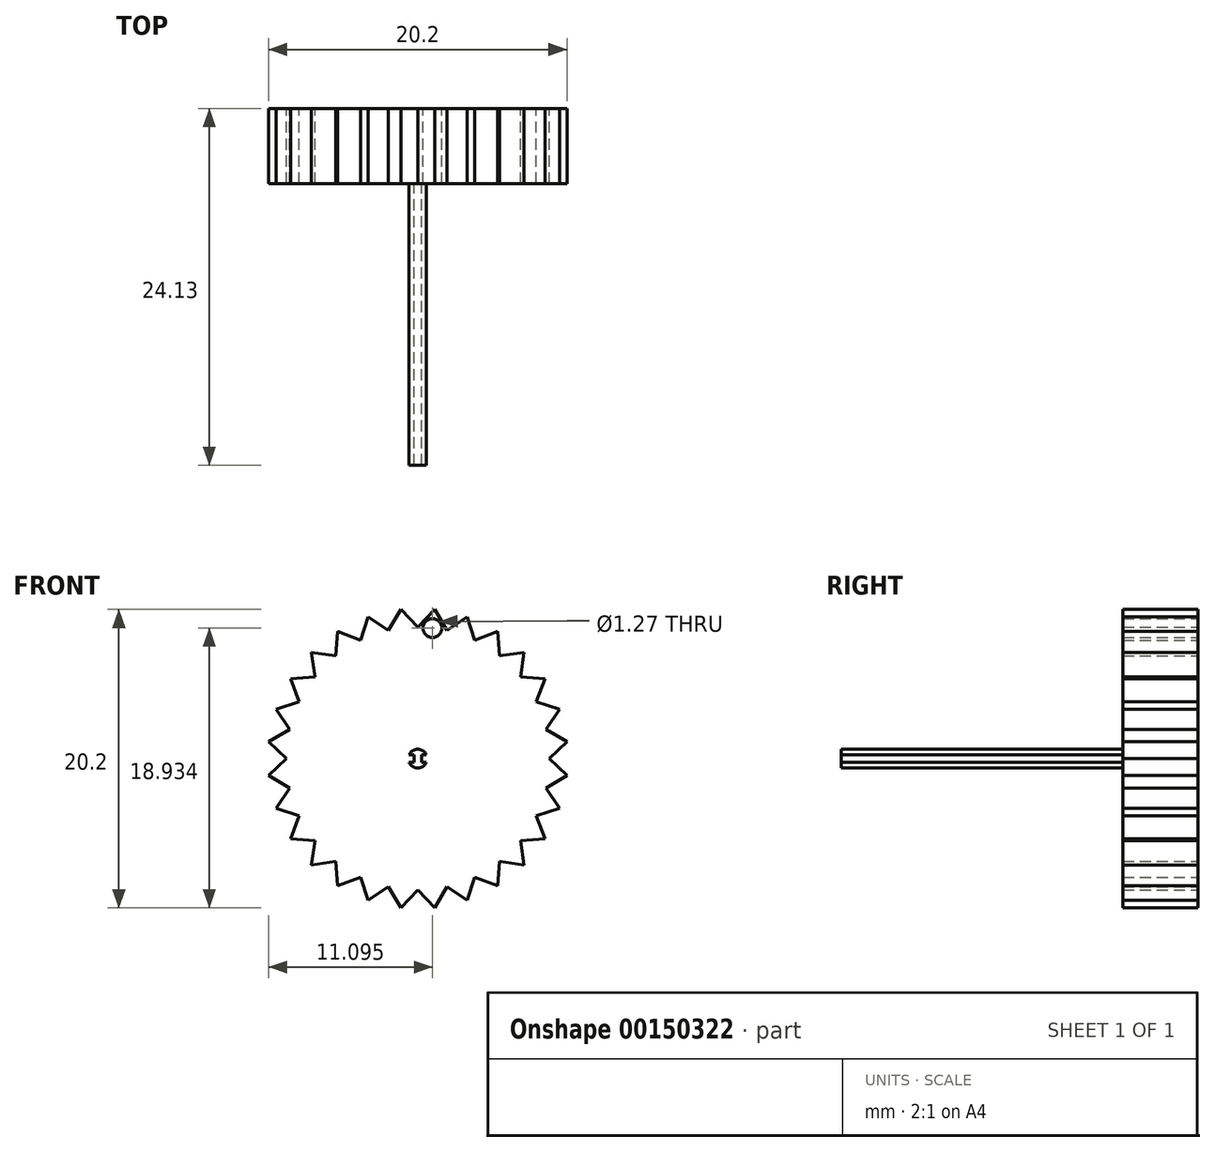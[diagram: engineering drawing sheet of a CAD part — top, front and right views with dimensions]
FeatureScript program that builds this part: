
annotation { "Feature Type Name" : "Feature", "Feature Type Description" : "" }
export const myFeature = defineFeature(function(context is Context, id is Id, definition is map)
    precondition{}
    {
        {
            var Q0;
            Q0=qCreatedBy(makeId("Front.planeOp"),FACE);
            var sketch = newSketch(context, id + "F0", { "sketchPlane" : qUnion([Q0])});
            skCircle(sketch, "E0", {"center": v(0, 0) * mm, "radius": 10.16 * mm});
            skCircle(sketch, "E1", {"center": v(0, 0) * mm, "radius": 8.9 * mm});
            skLineSegment(sketch, "E2", {"start": v(0, 0) * mm, "end": v(0, 8.9) * mm});
            skLineSegment(sketch, "E3", {"start": v(0, 8.9) * mm, "end": v(0, -8.9) * mm});
            skLineSegment(sketch, "E4", {"start": v(0, -8.9) * mm, "end": v(-1.14, -10.1) * mm});
            skLineSegment(sketch, "E5", {"start": v(-1.14, -10.1) * mm, "end": v(-1.98, -8.67) * mm});
            skLineSegment(sketch, "E6", {"start": v(-1.98, -8.67) * mm, "end": v(0, 0) * mm});
            skLineSegment(sketch, "E7", {"start": v(-1.14, -10.1) * mm, "end": v(0, 0) * mm});
            skLineSegment(sketch, "E8", {"start": v(0, 0) * mm, "end": v(-3.36, -9.59) * mm});
            skLineSegment(sketch, "E9", {"start": v(0, 0) * mm, "end": v(-3.86, -8) * mm});
            skLineSegment(sketch, "E10", {"start": v(-3.86, -8) * mm, "end": v(-3.36, -9.59) * mm});
            skLineSegment(sketch, "E11", {"start": v(-1.98, -8.67) * mm, "end": v(-3.36, -9.59) * mm});
            skLineSegment(sketch, "E12.MirrorCS", {"start": v(-3.86, -8) * mm, "end": v(-5.4, -8.6) * mm});
            skLineSegment(sketch, "E13.MirrorCS", {"start": v(0, 0) * mm, "end": v(-5.4, -8.6) * mm});
            skLineSegment(sketch, "E14.MirrorCS", {"start": v(-5.54, -6.95) * mm, "end": v(-5.4, -8.6) * mm});
            skLineSegment(sketch, "E15.MirrorCS", {"start": v(-7.18, -7.18) * mm, "end": v(-5.54, -6.95) * mm});
            skLineSegment(sketch, "E16.MirrorCS", {"start": v(-5.54, -6.95) * mm, "end": v(0, 0) * mm});
            skLineSegment(sketch, "E17.MirrorCS", {"start": v(-7.18, -7.18) * mm, "end": v(0, 0) * mm});
            skLineSegment(sketch, "E18.MirrorCS", {"start": v(-6.95, -5.54) * mm, "end": v(-7.18, -7.18) * mm});
            skLineSegment(sketch, "E19.MirrorCS", {"start": v(6.95, 5.54) * mm, "end": v(-6.95, -5.54) * mm});
            skLineSegment(sketch, "E20.MirrorCS", {"start": v(-6.95, -5.54) * mm, "end": v(-8.6, -5.4) * mm});
            skLineSegment(sketch, "E21.MirrorCS", {"start": v(-8.6, -5.4) * mm, "end": v(0, 0) * mm});
            skLineSegment(sketch, "E22.MirrorCS", {"start": v(-8.6, -5.4) * mm, "end": v(-8, -3.86) * mm});
            skLineSegment(sketch, "E23.MirrorCS", {"start": v(-8, -3.86) * mm, "end": v(0, 0) * mm});
            skLineSegment(sketch, "E24.MirrorCS", {"start": v(-8, -3.86) * mm, "end": v(-9.59, -3.36) * mm});
            skLineSegment(sketch, "E25.MirrorCS", {"start": v(0, 0) * mm, "end": v(-9.59, -3.36) * mm});
            skLineSegment(sketch, "E26.MirrorCS", {"start": v(-8.67, -1.98) * mm, "end": v(-9.59, -3.36) * mm});
            skLineSegment(sketch, "E27.MirrorCS", {"start": v(0, 0) * mm, "end": v(-8.67, -1.98) * mm});
            skLineSegment(sketch, "E28.MirrorCS", {"start": v(-8.67, -1.98) * mm, "end": v(-10.1, -1.14) * mm});
            skLineSegment(sketch, "E29.MirrorCS", {"start": v(0, 0) * mm, "end": v(-10.1, -1.14) * mm});
            skLineSegment(sketch, "E30.MirrorCS", {"start": v(-8.9, 0) * mm, "end": v(-10.1, -1.14) * mm});
            skLineSegment(sketch, "E31.MirrorCS", {"start": v(-8.9, 0) * mm, "end": v(0, 0) * mm});
            skLineSegment(sketch, "E32.MirrorCS", {"start": v(-10.1, 1.14) * mm, "end": v(-8.9, 0) * mm});
            skLineSegment(sketch, "E33.MirrorCS", {"start": v(-10.1, 1.14) * mm, "end": v(0, 0) * mm});
            skLineSegment(sketch, "E34.MirrorCS", {"start": v(-8.67, 1.98) * mm, "end": v(-10.1, 1.14) * mm});
            skLineSegment(sketch, "E35.MirrorCS", {"start": v(8.67, -1.98) * mm, "end": v(-8.67, 1.98) * mm});
            skLineSegment(sketch, "E36.MirrorCS", {"start": v(-8.67, 1.98) * mm, "end": v(-9.59, 3.36) * mm});
            skLineSegment(sketch, "E37.MirrorCS", {"start": v(-9.59, 3.36) * mm, "end": v(0, 0) * mm});
            skLineSegment(sketch, "E38.MirrorCS", {"start": v(-9.59, 3.36) * mm, "end": v(-8, 3.86) * mm});
            skLineSegment(sketch, "E39.MirrorCS", {"start": v(-8, 3.86) * mm, "end": v(0, 0) * mm});
            skLineSegment(sketch, "E40.MirrorCS", {"start": v(-8, 3.86) * mm, "end": v(-8.6, 5.4) * mm});
            skLineSegment(sketch, "E41.MirrorCS", {"start": v(0, 0) * mm, "end": v(-8.6, 5.4) * mm});
            skLineSegment(sketch, "E42.MirrorCS", {"start": v(-6.95, 5.54) * mm, "end": v(-8.6, 5.4) * mm});
            skLineSegment(sketch, "E43.MirrorCS", {"start": v(0, 0) * mm, "end": v(-6.95, 5.54) * mm});
            skLineSegment(sketch, "E44.MirrorCS", {"start": v(-6.95, 5.54) * mm, "end": v(-7.18, 7.18) * mm});
            skLineSegment(sketch, "E45.MirrorCS", {"start": v(0, 0) * mm, "end": v(-7.18, 7.18) * mm});
            skLineSegment(sketch, "E46.MirrorCS", {"start": v(-5.54, 6.95) * mm, "end": v(-7.18, 7.18) * mm});
            skLineSegment(sketch, "E47.MirrorCS", {"start": v(-5.54, 6.95) * mm, "end": v(0, 0) * mm});
            skLineSegment(sketch, "E48.MirrorCS", {"start": v(-5.4, 8.6) * mm, "end": v(-5.54, 6.95) * mm});
            skLineSegment(sketch, "E49.MirrorCS", {"start": v(-5.4, 8.6) * mm, "end": v(0, 0) * mm});
            skLineSegment(sketch, "E50.MirrorCS", {"start": v(-3.86, 8) * mm, "end": v(-5.4, 8.6) * mm});
            skLineSegment(sketch, "E51.MirrorCS", {"start": v(3.86, -8) * mm, "end": v(-3.86, 8) * mm});
            skLineSegment(sketch, "E52.MirrorCS", {"start": v(-3.86, 8) * mm, "end": v(-3.36, 9.59) * mm});
            skLineSegment(sketch, "E53.MirrorCS", {"start": v(-3.36, 9.59) * mm, "end": v(0, 0) * mm});
            skLineSegment(sketch, "E54.MirrorCS", {"start": v(-3.36, 9.59) * mm, "end": v(-1.98, 8.67) * mm});
            skLineSegment(sketch, "E55.MirrorCS", {"start": v(-1.98, 8.67) * mm, "end": v(0, 0) * mm});
            skLineSegment(sketch, "E56.MirrorCS", {"start": v(-1.98, 8.67) * mm, "end": v(-1.14, 10.1) * mm});
            skLineSegment(sketch, "E57.MirrorCS", {"start": v(0, 0) * mm, "end": v(-1.14, 10.1) * mm});
            skLineSegment(sketch, "E58.MirrorCS", {"start": v(0, 8.89) * mm, "end": v(-1.14, 10.1) * mm});
            skLineSegment(sketch, "E59.MirrorCS", {"start": v(0, 0) * mm, "end": v(0, 8.89) * mm});
            skLineSegment(sketch, "E60.MirrorCS", {"start": v(0, 8.89) * mm, "end": v(1.14, 10.1) * mm});
            skLineSegment(sketch, "E61.MirrorCS", {"start": v(0, 0) * mm, "end": v(1.14, 10.1) * mm});
            skLineSegment(sketch, "E62.MirrorCS", {"start": v(1.98, 8.67) * mm, "end": v(1.14, 10.1) * mm});
            skLineSegment(sketch, "E63.MirrorCS", {"start": v(1.98, 8.67) * mm, "end": v(0, 0) * mm});
            skLineSegment(sketch, "E64.MirrorCS", {"start": v(3.36, 9.59) * mm, "end": v(1.98, 8.67) * mm});
            skLineSegment(sketch, "E65.MirrorCS", {"start": v(3.36, 9.59) * mm, "end": v(0, 0) * mm});
            skLineSegment(sketch, "E66.MirrorCS", {"start": v(3.86, 8) * mm, "end": v(3.36, 9.59) * mm});
            skLineSegment(sketch, "E67.MirrorCS", {"start": v(-3.86, -8) * mm, "end": v(3.86, 8) * mm});
            skLineSegment(sketch, "E68.MirrorCS", {"start": v(3.86, 8) * mm, "end": v(5.4, 8.6) * mm});
            skLineSegment(sketch, "E69.MirrorCS", {"start": v(5.4, 8.6) * mm, "end": v(0, 0) * mm});
            skLineSegment(sketch, "E70.MirrorCS", {"start": v(5.4, 8.6) * mm, "end": v(5.54, 6.95) * mm});
            skLineSegment(sketch, "E71.MirrorCS", {"start": v(5.54, 6.95) * mm, "end": v(0, 0) * mm});
            skLineSegment(sketch, "E72.MirrorCS", {"start": v(5.54, 6.95) * mm, "end": v(7.18, 7.18) * mm});
            skLineSegment(sketch, "E73.MirrorCS", {"start": v(0, 0) * mm, "end": v(7.18, 7.18) * mm});
            skLineSegment(sketch, "E74.MirrorCS", {"start": v(6.95, 5.54) * mm, "end": v(7.18, 7.18) * mm});
            skLineSegment(sketch, "E75.MirrorCS", {"start": v(6.95, 5.54) * mm, "end": v(8.6, 5.4) * mm});
            skLineSegment(sketch, "E76.MirrorCS", {"start": v(0, 0) * mm, "end": v(8.6, 5.4) * mm});
            skLineSegment(sketch, "E77.MirrorCS", {"start": v(8, 3.86) * mm, "end": v(8.6, 5.4) * mm});
            skLineSegment(sketch, "E78.MirrorCS", {"start": v(8, 3.86) * mm, "end": v(0, 0) * mm});
            skLineSegment(sketch, "E79.MirrorCS", {"start": v(9.59, 3.36) * mm, "end": v(8, 3.86) * mm});
            skLineSegment(sketch, "E80.MirrorCS", {"start": v(9.59, 3.36) * mm, "end": v(0, 0) * mm});
            skLineSegment(sketch, "E81.MirrorCS", {"start": v(8.67, 1.98) * mm, "end": v(9.59, 3.36) * mm});
            skLineSegment(sketch, "E82.MirrorCS", {"start": v(-8.67, -1.98) * mm, "end": v(8.67, 1.98) * mm});
            skLineSegment(sketch, "E83.MirrorCS", {"start": v(8.67, 1.98) * mm, "end": v(10.1, 1.14) * mm});
            skLineSegment(sketch, "E84.MirrorCS", {"start": v(10.1, 1.14) * mm, "end": v(8.9, 0) * mm});
            skLineSegment(sketch, "E85.MirrorCS", {"start": v(10.1, 1.14) * mm, "end": v(0, 0) * mm});
            skLineSegment(sketch, "E86.MirrorCS", {"start": v(8.9, 0) * mm, "end": v(0, 0) * mm});
            skLineSegment(sketch, "E87.MirrorCS", {"start": v(8.9, 0) * mm, "end": v(10.1, -1.14) * mm});
            skLineSegment(sketch, "E88.MirrorCS", {"start": v(0, 0) * mm, "end": v(10.1, -1.14) * mm});
            skLineSegment(sketch, "E89.MirrorCS", {"start": v(8.67, -1.98) * mm, "end": v(10.1, -1.14) * mm});
            skLineSegment(sketch, "E90.MirrorCS", {"start": v(0, 0) * mm, "end": v(8.67, -1.98) * mm});
            skLineSegment(sketch, "E91.MirrorCS", {"start": v(8.67, -1.98) * mm, "end": v(9.59, -3.36) * mm});
            skLineSegment(sketch, "E92.MirrorCS", {"start": v(0, 0) * mm, "end": v(9.59, -3.36) * mm});
            skLineSegment(sketch, "E93.MirrorCS", {"start": v(8, -3.86) * mm, "end": v(9.59, -3.36) * mm});
            skLineSegment(sketch, "E94.MirrorCS", {"start": v(8, -3.86) * mm, "end": v(0, 0) * mm});
            skLineSegment(sketch, "E95.MirrorCS", {"start": v(8.6, -5.4) * mm, "end": v(8, -3.86) * mm});
            skLineSegment(sketch, "E96.MirrorCS", {"start": v(8.6, -5.4) * mm, "end": v(0, 0) * mm});
            skLineSegment(sketch, "E97.MirrorCS", {"start": v(6.95, -5.54) * mm, "end": v(8.6, -5.4) * mm});
            skLineSegment(sketch, "E98.MirrorCS", {"start": v(-6.95, 5.54) * mm, "end": v(6.95, -5.54) * mm});
            skLineSegment(sketch, "E99.MirrorCS", {"start": v(6.95, -5.54) * mm, "end": v(7.18, -7.18) * mm});
            skLineSegment(sketch, "E100.MirrorCS", {"start": v(7.18, -7.18) * mm, "end": v(0, 0) * mm});
            skLineSegment(sketch, "E101.MirrorCS", {"start": v(7.18, -7.18) * mm, "end": v(5.54, -6.95) * mm});
            skLineSegment(sketch, "E102.MirrorCS", {"start": v(5.54, -6.95) * mm, "end": v(0, 0) * mm});
            skLineSegment(sketch, "E103.MirrorCS", {"start": v(5.54, -6.95) * mm, "end": v(5.4, -8.6) * mm});
            skLineSegment(sketch, "E104.MirrorCS", {"start": v(0, 0) * mm, "end": v(5.4, -8.6) * mm});
            skLineSegment(sketch, "E105.MirrorCS", {"start": v(3.86, -8) * mm, "end": v(5.4, -8.6) * mm});
            skLineSegment(sketch, "E106.MirrorCS", {"start": v(0, 0) * mm, "end": v(3.86, -8) * mm});
            skLineSegment(sketch, "E107.MirrorCS", {"start": v(3.86, -8) * mm, "end": v(3.36, -9.59) * mm});
            skLineSegment(sketch, "E108.MirrorCS", {"start": v(1.98, -8.67) * mm, "end": v(3.36, -9.59) * mm});
            skLineSegment(sketch, "E109.MirrorCS", {"start": v(0, 0) * mm, "end": v(3.36, -9.59) * mm});
            skLineSegment(sketch, "E110.MirrorCS", {"start": v(1.98, -8.67) * mm, "end": v(0, 0) * mm});
            skLineSegment(sketch, "E111.MirrorCS", {"start": v(1.14, -10.1) * mm, "end": v(1.98, -8.67) * mm});
            skLineSegment(sketch, "E112.MirrorCS", {"start": v(1.14, -10.1) * mm, "end": v(0, 0) * mm});
            skLineSegment(sketch, "E113.MirrorCS", {"start": v(0, -8.9) * mm, "end": v(1.14, -10.1) * mm});
            skSolve(sketch);
        }
        {
            var Q0;
            {var subQ0=sQuery(id+"F0.wireOp",EDGE,"E51.MirrorCS");Q0=makeQuery(id+"F0.imprint","IMPRINT",FACE,{"disambiguationData":[TD([[makeQuery(id+"F0.imprint","IMPRINT",EDGE,{"derivedFrom":subQ0}),1.0]])]});}
            var Q1;
            {var subQ0=sQuery(id+"F0.wireOp",EDGE,"E47.MirrorCS");Q1=makeQuery(id+"F0.imprint","IMPRINT",FACE,{"disambiguationData":[TD([[makeQuery(id+"F0.imprint","IMPRINT",EDGE,{"derivedFrom":subQ0}),1.0]])]});}
            var Q2;
            {var subQ0=sQuery(id+"F0.wireOp",EDGE,"E48.MirrorCS");Q2=makeQuery(id+"F0.imprint","IMPRINT",FACE,{"disambiguationData":[TD([[makeQuery(id+"F0.imprint","IMPRINT",EDGE,{"derivedFrom":subQ0}),1.0]])]});}
            var Q3;
            {var subQ0=sQuery(id+"F0.wireOp",EDGE,"E50.MirrorCS");Q3=makeQuery(id+"F0.imprint","IMPRINT",FACE,{"disambiguationData":[TD([[makeQuery(id+"F0.imprint","IMPRINT",EDGE,{"derivedFrom":subQ0}),1.0]])]});}
            var Q4;
            {var subQ0=sQuery(id+"F0.wireOp",EDGE,"E52.MirrorCS");Q4=makeQuery(id+"F0.imprint","IMPRINT",FACE,{"disambiguationData":[TD([[makeQuery(id+"F0.imprint","IMPRINT",EDGE,{"derivedFrom":subQ0}),-1.0]])]});}
            var Q5;
            {var subQ0=sQuery(id+"F0.wireOp",EDGE,"E54.MirrorCS");Q5=makeQuery(id+"F0.imprint","IMPRINT",FACE,{"disambiguationData":[TD([[makeQuery(id+"F0.imprint","IMPRINT",EDGE,{"derivedFrom":subQ0}),-1.0]])]});}
            var Q6;
            {var subQ0=sQuery(id+"F0.wireOp",EDGE,"E55.MirrorCS");Q6=makeQuery(id+"F0.imprint","IMPRINT",FACE,{"disambiguationData":[TD([[makeQuery(id+"F0.imprint","IMPRINT",EDGE,{"derivedFrom":subQ0}),-1.0]])]});}
            var Q7;
            {var subQ0=sQuery(id+"F0.wireOp",EDGE,"E51.MirrorCS");Q7=makeQuery(id+"F0.imprint","IMPRINT",FACE,{"disambiguationData":[TD([[makeQuery(id+"F0.imprint","IMPRINT",EDGE,{"derivedFrom":subQ0}),-1.0]])]});}
            var Q8;
            {var subQ1=sQuery(id+"F0.wireOp",EDGE,"E1");var subQ3=sQuery(id+"F0.wireOp",EDGE,"E57.MirrorCS");var subQ4=makeQuery(id+"F0.imprint","INTERSECT",VERTEX,{"derivedFrom":[subQ1,subQ3]});Q8=makeQuery(id+"F0.imprint","IMPRINT",FACE,{"disambiguationData":[TD([[makeQuery(id+"F0.imprint","IMPRINT",EDGE,{"disambiguationData":[TD([[subQ4,1.0]])],"derivedFrom":subQ1}),1.0]])]});}
            var Q9;
            {var subQ0=sQuery(id+"F0.wireOp",EDGE,"E58.MirrorCS");Q9=makeQuery(id+"F0.imprint","IMPRINT",FACE,{"disambiguationData":[TD([[makeQuery(id+"F0.imprint","IMPRINT",EDGE,{"derivedFrom":subQ0}),1.0]])]});}
            var Q10;
            {var subQ0=sQuery(id+"F0.wireOp",EDGE,"E56.MirrorCS");Q10=makeQuery(id+"F0.imprint","IMPRINT",FACE,{"disambiguationData":[TD([[makeQuery(id+"F0.imprint","IMPRINT",EDGE,{"derivedFrom":subQ0}),-1.0]])]});}
            var Q11;
            {var subQ0=sQuery(id+"F0.wireOp",EDGE,"E55.MirrorCS");Q11=makeQuery(id+"F0.imprint","IMPRINT",FACE,{"disambiguationData":[TD([[makeQuery(id+"F0.imprint","IMPRINT",EDGE,{"derivedFrom":subQ0}),1.0]])]});}
            var Q12;
            {var subQ0=sQuery(id+"F0.wireOp",EDGE,"E47.MirrorCS");Q12=makeQuery(id+"F0.imprint","IMPRINT",FACE,{"disambiguationData":[TD([[makeQuery(id+"F0.imprint","IMPRINT",EDGE,{"derivedFrom":subQ0}),-1.0]])]});}
            var Q13;
            {var subQ0=sQuery(id+"F0.wireOp",EDGE,"E46.MirrorCS");Q13=makeQuery(id+"F0.imprint","IMPRINT",FACE,{"disambiguationData":[TD([[makeQuery(id+"F0.imprint","IMPRINT",EDGE,{"derivedFrom":subQ0}),1.0]])]});}
            var Q14;
            {var subQ1=sQuery(id+"F0.wireOp",EDGE,"E1");var subQ3=sQuery(id+"F0.wireOp",EDGE,"E45.MirrorCS");var subQ4=makeQuery(id+"F0.imprint","INTERSECT",VERTEX,{"derivedFrom":[subQ1,subQ3]});Q14=makeQuery(id+"F0.imprint","IMPRINT",FACE,{"disambiguationData":[TD([[makeQuery(id+"F0.imprint","IMPRINT",EDGE,{"disambiguationData":[TD([[subQ4,-1.0]])],"derivedFrom":subQ1}),1.0]])]});}
            var Q15;
            {var subQ0=sQuery(id+"F0.wireOp",EDGE,"E44.MirrorCS");Q15=makeQuery(id+"F0.imprint","IMPRINT",FACE,{"disambiguationData":[TD([[makeQuery(id+"F0.imprint","IMPRINT",EDGE,{"derivedFrom":subQ0}),-1.0]])]});}
            var Q16;
            {var subQ1=sQuery(id+"F0.wireOp",EDGE,"E1");var subQ3=sQuery(id+"F0.wireOp",EDGE,"E41.MirrorCS");var subQ4=makeQuery(id+"F0.imprint","INTERSECT",VERTEX,{"derivedFrom":[subQ1,subQ3]});Q16=makeQuery(id+"F0.imprint","IMPRINT",FACE,{"disambiguationData":[TD([[makeQuery(id+"F0.imprint","IMPRINT",EDGE,{"disambiguationData":[TD([[subQ4,1.0]])],"derivedFrom":subQ1}),1.0]])]});}
            var Q17;
            {var subQ0=sQuery(id+"F0.wireOp",EDGE,"E42.MirrorCS");Q17=makeQuery(id+"F0.imprint","IMPRINT",FACE,{"disambiguationData":[TD([[makeQuery(id+"F0.imprint","IMPRINT",EDGE,{"derivedFrom":subQ0}),1.0]])]});}
            var Q18;
            {var subQ0=sQuery(id+"F0.wireOp",EDGE,"E40.MirrorCS");Q18=makeQuery(id+"F0.imprint","IMPRINT",FACE,{"disambiguationData":[TD([[makeQuery(id+"F0.imprint","IMPRINT",EDGE,{"derivedFrom":subQ0}),-1.0]])]});}
            var Q19;
            {var subQ0=sQuery(id+"F0.wireOp",EDGE,"E39.MirrorCS");Q19=makeQuery(id+"F0.imprint","IMPRINT",FACE,{"disambiguationData":[TD([[makeQuery(id+"F0.imprint","IMPRINT",EDGE,{"derivedFrom":subQ0}),1.0]])]});}
            var Q20;
            {var subQ0=sQuery(id+"F0.wireOp",EDGE,"E39.MirrorCS");Q20=makeQuery(id+"F0.imprint","IMPRINT",FACE,{"disambiguationData":[TD([[makeQuery(id+"F0.imprint","IMPRINT",EDGE,{"derivedFrom":subQ0}),-1.0]])]});}
            var Q21;
            {var subQ0=sQuery(id+"F0.wireOp",EDGE,"E38.MirrorCS");Q21=makeQuery(id+"F0.imprint","IMPRINT",FACE,{"disambiguationData":[TD([[makeQuery(id+"F0.imprint","IMPRINT",EDGE,{"derivedFrom":subQ0}),-1.0]])]});}
            var Q22;
            {var subQ0=sQuery(id+"F0.wireOp",EDGE,"E36.MirrorCS");Q22=makeQuery(id+"F0.imprint","IMPRINT",FACE,{"disambiguationData":[TD([[makeQuery(id+"F0.imprint","IMPRINT",EDGE,{"derivedFrom":subQ0}),-1.0]])]});}
            var Q23;
            {var subQ0=sQuery(id+"F0.wireOp",EDGE,"E35.MirrorCS");Q23=makeQuery(id+"F0.imprint","IMPRINT",FACE,{"disambiguationData":[TD([[makeQuery(id+"F0.imprint","IMPRINT",EDGE,{"derivedFrom":subQ0}),-1.0]])]});}
            var Q24;
            {var subQ0=sQuery(id+"F0.wireOp",EDGE,"E35.MirrorCS");Q24=makeQuery(id+"F0.imprint","IMPRINT",FACE,{"disambiguationData":[TD([[makeQuery(id+"F0.imprint","IMPRINT",EDGE,{"derivedFrom":subQ0}),1.0]])]});}
            var Q25;
            {var subQ0=sQuery(id+"F0.wireOp",EDGE,"E34.MirrorCS");Q25=makeQuery(id+"F0.imprint","IMPRINT",FACE,{"disambiguationData":[TD([[makeQuery(id+"F0.imprint","IMPRINT",EDGE,{"derivedFrom":subQ0}),1.0]])]});}
            var Q26;
            {var subQ0=sQuery(id+"F0.wireOp",EDGE,"E32.MirrorCS");Q26=makeQuery(id+"F0.imprint","IMPRINT",FACE,{"disambiguationData":[TD([[makeQuery(id+"F0.imprint","IMPRINT",EDGE,{"derivedFrom":subQ0}),1.0]])]});}
            var Q27;
            {var subQ0=sQuery(id+"F0.wireOp",EDGE,"E31.MirrorCS");Q27=makeQuery(id+"F0.imprint","IMPRINT",FACE,{"disambiguationData":[TD([[makeQuery(id+"F0.imprint","IMPRINT",EDGE,{"derivedFrom":subQ0}),1.0]])]});}
            var Q28;
            {var subQ0=sQuery(id+"F0.wireOp",EDGE,"E31.MirrorCS");Q28=makeQuery(id+"F0.imprint","IMPRINT",FACE,{"disambiguationData":[TD([[makeQuery(id+"F0.imprint","IMPRINT",EDGE,{"derivedFrom":subQ0}),-1.0]])]});}
            var Q29;
            {var subQ0=sQuery(id+"F0.wireOp",EDGE,"E30.MirrorCS");Q29=makeQuery(id+"F0.imprint","IMPRINT",FACE,{"disambiguationData":[TD([[makeQuery(id+"F0.imprint","IMPRINT",EDGE,{"derivedFrom":subQ0}),1.0]])]});}
            var Q30;
            {var subQ0=sQuery(id+"F0.wireOp",EDGE,"E28.MirrorCS");Q30=makeQuery(id+"F0.imprint","IMPRINT",FACE,{"disambiguationData":[TD([[makeQuery(id+"F0.imprint","IMPRINT",EDGE,{"derivedFrom":subQ0}),-1.0]])]});}
            var Q31;
            {var subQ1=sQuery(id+"F0.wireOp",EDGE,"E1");var subQ3=sQuery(id+"F0.wireOp",EDGE,"E29.MirrorCS");var subQ4=makeQuery(id+"F0.imprint","INTERSECT",VERTEX,{"derivedFrom":[subQ1,subQ3]});Q31=makeQuery(id+"F0.imprint","IMPRINT",FACE,{"disambiguationData":[TD([[makeQuery(id+"F0.imprint","IMPRINT",EDGE,{"disambiguationData":[TD([[subQ4,-1.0]])],"derivedFrom":subQ1}),1.0]])]});}
            var Q32;
            {var subQ1=sQuery(id+"F0.wireOp",EDGE,"E1");var subQ3=sQuery(id+"F0.wireOp",EDGE,"E25.MirrorCS");var subQ4=makeQuery(id+"F0.imprint","INTERSECT",VERTEX,{"derivedFrom":[subQ1,subQ3]});Q32=makeQuery(id+"F0.imprint","IMPRINT",FACE,{"disambiguationData":[TD([[makeQuery(id+"F0.imprint","IMPRINT",EDGE,{"disambiguationData":[TD([[subQ4,1.0]])],"derivedFrom":subQ1}),1.0]])]});}
            var Q33;
            {var subQ0=sQuery(id+"F0.wireOp",EDGE,"E26.MirrorCS");Q33=makeQuery(id+"F0.imprint","IMPRINT",FACE,{"disambiguationData":[TD([[makeQuery(id+"F0.imprint","IMPRINT",EDGE,{"derivedFrom":subQ0}),1.0]])]});}
            var Q34;
            {var subQ0=sQuery(id+"F0.wireOp",EDGE,"E24.MirrorCS");Q34=makeQuery(id+"F0.imprint","IMPRINT",FACE,{"disambiguationData":[TD([[makeQuery(id+"F0.imprint","IMPRINT",EDGE,{"derivedFrom":subQ0}),-1.0]])]});}
            var Q35;
            {var subQ0=sQuery(id+"F0.wireOp",EDGE,"E23.MirrorCS");Q35=makeQuery(id+"F0.imprint","IMPRINT",FACE,{"disambiguationData":[TD([[makeQuery(id+"F0.imprint","IMPRINT",EDGE,{"derivedFrom":subQ0}),1.0]])]});}
            var Q36;
            {var subQ0=sQuery(id+"F0.wireOp",EDGE,"E23.MirrorCS");Q36=makeQuery(id+"F0.imprint","IMPRINT",FACE,{"disambiguationData":[TD([[makeQuery(id+"F0.imprint","IMPRINT",EDGE,{"derivedFrom":subQ0}),-1.0]])]});}
            var Q37;
            {var subQ0=sQuery(id+"F0.wireOp",EDGE,"E22.MirrorCS");Q37=makeQuery(id+"F0.imprint","IMPRINT",FACE,{"disambiguationData":[TD([[makeQuery(id+"F0.imprint","IMPRINT",EDGE,{"derivedFrom":subQ0}),-1.0]])]});}
            var Q38;
            {var subQ0=sQuery(id+"F0.wireOp",EDGE,"E20.MirrorCS");Q38=makeQuery(id+"F0.imprint","IMPRINT",FACE,{"disambiguationData":[TD([[makeQuery(id+"F0.imprint","IMPRINT",EDGE,{"derivedFrom":subQ0}),-1.0]])]});}
            var Q39;
            {var subQ1=sQuery(id+"F0.wireOp",EDGE,"E1");var subQ3=sQuery(id+"F0.wireOp",EDGE,"E21.MirrorCS");var subQ4=makeQuery(id+"F0.imprint","INTERSECT",VERTEX,{"derivedFrom":[subQ1,subQ3]});Q39=makeQuery(id+"F0.imprint","IMPRINT",FACE,{"disambiguationData":[TD([[makeQuery(id+"F0.imprint","IMPRINT",EDGE,{"disambiguationData":[TD([[subQ4,-1.0]])],"derivedFrom":subQ1}),1.0]])]});}
            var Q40;
            {var subQ1=sQuery(id+"F0.wireOp",EDGE,"E1");var subQ3=sQuery(id+"F0.wireOp",EDGE,"E17.MirrorCS");var subQ4=makeQuery(id+"F0.imprint","INTERSECT",VERTEX,{"derivedFrom":[subQ1,subQ3]});Q40=makeQuery(id+"F0.imprint","IMPRINT",FACE,{"disambiguationData":[TD([[makeQuery(id+"F0.imprint","IMPRINT",EDGE,{"disambiguationData":[TD([[subQ4,1.0]])],"derivedFrom":subQ1}),1.0]])]});}
            var Q41;
            {var subQ0=sQuery(id+"F0.wireOp",EDGE,"E16.MirrorCS");Q41=makeQuery(id+"F0.imprint","IMPRINT",FACE,{"disambiguationData":[TD([[makeQuery(id+"F0.imprint","IMPRINT",EDGE,{"derivedFrom":subQ0}),1.0]])]});}
            var Q42;
            {var subQ0=sQuery(id+"F0.wireOp",EDGE,"E16.MirrorCS");Q42=makeQuery(id+"F0.imprint","IMPRINT",FACE,{"disambiguationData":[TD([[makeQuery(id+"F0.imprint","IMPRINT",EDGE,{"derivedFrom":subQ0}),-1.0]])]});}
            var Q43;
            {var subQ0=sQuery(id+"F0.wireOp",EDGE,"E18.MirrorCS");Q43=makeQuery(id+"F0.imprint","IMPRINT",FACE,{"disambiguationData":[TD([[makeQuery(id+"F0.imprint","IMPRINT",EDGE,{"derivedFrom":subQ0}),1.0]])]});}
            var Q44;
            {var subQ0=sQuery(id+"F0.wireOp",EDGE,"E15.MirrorCS");Q44=makeQuery(id+"F0.imprint","IMPRINT",FACE,{"disambiguationData":[TD([[makeQuery(id+"F0.imprint","IMPRINT",EDGE,{"derivedFrom":subQ0}),1.0]])]});}
            var Q45;
            {var subQ0=sQuery(id+"F0.wireOp",EDGE,"E14.MirrorCS");Q45=makeQuery(id+"F0.imprint","IMPRINT",FACE,{"disambiguationData":[TD([[makeQuery(id+"F0.imprint","IMPRINT",EDGE,{"derivedFrom":subQ0}),1.0]])]});}
            var Q46;
            {var subQ0=sQuery(id+"F0.wireOp",EDGE,"E12.MirrorCS");Q46=makeQuery(id+"F0.imprint","IMPRINT",FACE,{"disambiguationData":[TD([[makeQuery(id+"F0.imprint","IMPRINT",EDGE,{"derivedFrom":subQ0}),-1.0]])]});}
            var Q47;
            {var subQ1=sQuery(id+"F0.wireOp",EDGE,"E1");var subQ3=sQuery(id+"F0.wireOp",EDGE,"E8");var subQ4=makeQuery(id+"F0.imprint","INTERSECT",VERTEX,{"derivedFrom":[subQ1,subQ3]});Q47=makeQuery(id+"F0.imprint","IMPRINT",FACE,{"disambiguationData":[TD([[makeQuery(id+"F0.imprint","IMPRINT",EDGE,{"disambiguationData":[TD([[subQ4,1.0]])],"derivedFrom":subQ1}),1.0]])]});}
            var Q48;
            {var subQ0=sQuery(id+"F0.wireOp",EDGE,"E10");Q48=makeQuery(id+"F0.imprint","IMPRINT",FACE,{"disambiguationData":[TD([[makeQuery(id+"F0.imprint","IMPRINT",EDGE,{"derivedFrom":subQ0}),1.0]])]});}
            var Q49;
            {var subQ0=sQuery(id+"F0.wireOp",EDGE,"E11");Q49=makeQuery(id+"F0.imprint","IMPRINT",FACE,{"disambiguationData":[TD([[makeQuery(id+"F0.imprint","IMPRINT",EDGE,{"derivedFrom":subQ0}),-1.0]])]});}
            var Q50;
            {var subQ0=sQuery(id+"F0.wireOp",EDGE,"E6");Q50=makeQuery(id+"F0.imprint","IMPRINT",FACE,{"disambiguationData":[TD([[makeQuery(id+"F0.imprint","IMPRINT",EDGE,{"derivedFrom":subQ0}),1.0]])]});}
            var Q51;
            {var subQ0=sQuery(id+"F0.wireOp",EDGE,"E6");Q51=makeQuery(id+"F0.imprint","IMPRINT",FACE,{"disambiguationData":[TD([[makeQuery(id+"F0.imprint","IMPRINT",EDGE,{"derivedFrom":subQ0}),-1.0]])]});}
            var Q52;
            {var subQ0=sQuery(id+"F0.wireOp",EDGE,"E4");Q52=makeQuery(id+"F0.imprint","IMPRINT",FACE,{"disambiguationData":[TD([[makeQuery(id+"F0.imprint","IMPRINT",EDGE,{"derivedFrom":subQ0}),-1.0]])]});}
            var Q53;
            {var subQ0=sQuery(id+"F0.wireOp",EDGE,"E5");Q53=makeQuery(id+"F0.imprint","IMPRINT",FACE,{"disambiguationData":[TD([[makeQuery(id+"F0.imprint","IMPRINT",EDGE,{"derivedFrom":subQ0}),-1.0]])]});}
            var Q54;
            {var subQ1=sQuery(id+"F0.wireOp",EDGE,"E1");var subQ3=sQuery(id+"F0.wireOp",EDGE,"E7");var subQ4=makeQuery(id+"F0.imprint","INTERSECT",VERTEX,{"derivedFrom":[subQ1,subQ3]});Q54=makeQuery(id+"F0.imprint","IMPRINT",FACE,{"disambiguationData":[TD([[makeQuery(id+"F0.imprint","IMPRINT",EDGE,{"disambiguationData":[TD([[subQ4,-1.0]])],"derivedFrom":subQ1}),1.0]])]});}
            var Q55;
            {var subQ1=sQuery(id+"F0.wireOp",EDGE,"E1");var subQ3=sQuery(id+"F0.wireOp",EDGE,"E13.MirrorCS");var subQ4=makeQuery(id+"F0.imprint","INTERSECT",VERTEX,{"derivedFrom":[subQ1,subQ3]});Q55=makeQuery(id+"F0.imprint","IMPRINT",FACE,{"disambiguationData":[TD([[makeQuery(id+"F0.imprint","IMPRINT",EDGE,{"disambiguationData":[TD([[subQ4,-1.0]])],"derivedFrom":subQ1}),1.0]])]});}
            extrude(context, id + "F1", {"entities" : qUnion([Q0, Q1, Q2, Q3, Q4, Q5, Q6, Q7, Q8, Q9, Q10, Q11, Q12, Q13, Q14, Q15, Q16, Q17, Q18, Q19, Q20, Q21, Q22, Q23, Q24, Q25, Q26, Q27, Q28, Q29, Q30, Q31, Q32, Q33, Q34, Q35, Q36, Q37, Q38, Q39, Q40, Q41, Q42, Q43, Q44, Q45, Q46, Q47, Q48, Q49, Q50, Q51, Q52, Q53, Q54, Q55]), "depth" : 5.08 * mm});
        }
        {
            var Q0;
            Q0=makeQuery(id+"F1.opExtrude","SWEPT_BODY",BODY,{"disambiguationData":[OSD([sQuery(id+"F0.wireOp",EDGE,"E4"),sQuery(id+"F0.wireOp",EDGE,"E5"),sQuery(id+"F0.wireOp",EDGE,"E10"),sQuery(id+"F0.wireOp",EDGE,"E11"),sQuery(id+"F0.wireOp",EDGE,"E12.MirrorCS"),sQuery(id+"F0.wireOp",EDGE,"E14.MirrorCS"),sQuery(id+"F0.wireOp",EDGE,"E15.MirrorCS"),sQuery(id+"F0.wireOp",EDGE,"E18.MirrorCS"),sQuery(id+"F0.wireOp",EDGE,"E20.MirrorCS"),sQuery(id+"F0.wireOp",EDGE,"E22.MirrorCS"),sQuery(id+"F0.wireOp",EDGE,"E24.MirrorCS"),sQuery(id+"F0.wireOp",EDGE,"E26.MirrorCS"),sQuery(id+"F0.wireOp",EDGE,"E28.MirrorCS"),sQuery(id+"F0.wireOp",EDGE,"E30.MirrorCS"),sQuery(id+"F0.wireOp",EDGE,"E32.MirrorCS"),sQuery(id+"F0.wireOp",EDGE,"E34.MirrorCS"),sQuery(id+"F0.wireOp",EDGE,"E36.MirrorCS"),sQuery(id+"F0.wireOp",EDGE,"E38.MirrorCS"),sQuery(id+"F0.wireOp",EDGE,"E40.MirrorCS"),sQuery(id+"F0.wireOp",EDGE,"E42.MirrorCS"),sQuery(id+"F0.wireOp",EDGE,"E44.MirrorCS"),sQuery(id+"F0.wireOp",EDGE,"E46.MirrorCS"),sQuery(id+"F0.wireOp",EDGE,"E48.MirrorCS"),sQuery(id+"F0.wireOp",EDGE,"E50.MirrorCS"),sQuery(id+"F0.wireOp",EDGE,"E52.MirrorCS"),sQuery(id+"F0.wireOp",EDGE,"E54.MirrorCS"),sQuery(id+"F0.wireOp",EDGE,"E56.MirrorCS"),sQuery(id+"F0.wireOp",EDGE,"E58.MirrorCS"),sQuery(id+"F0.wireOp",EDGE,"E3")])]});
            var Q1;
            Q1=qCreatedBy(makeId("Right.planeOp"),FACE);
            mirror(context, id + "F2", {"operationType" : NewBodyOperationType.ADD, "entities" : qUnion([Q0]), "mirrorPlane" : qUnion([Q1])});
        }
        {
            var Q0;
            {var subQ0=makeQuery(id+"F1.opExtrude","CAP_FACE",FACE,{"disambiguationData":[OSD([sQuery(id+"F0.wireOp",EDGE,"E4"),sQuery(id+"F0.wireOp",EDGE,"E5"),sQuery(id+"F0.wireOp",EDGE,"E10"),sQuery(id+"F0.wireOp",EDGE,"E11"),sQuery(id+"F0.wireOp",EDGE,"E12.MirrorCS"),sQuery(id+"F0.wireOp",EDGE,"E14.MirrorCS"),sQuery(id+"F0.wireOp",EDGE,"E15.MirrorCS"),sQuery(id+"F0.wireOp",EDGE,"E18.MirrorCS"),sQuery(id+"F0.wireOp",EDGE,"E20.MirrorCS"),sQuery(id+"F0.wireOp",EDGE,"E22.MirrorCS"),sQuery(id+"F0.wireOp",EDGE,"E24.MirrorCS"),sQuery(id+"F0.wireOp",EDGE,"E26.MirrorCS"),sQuery(id+"F0.wireOp",EDGE,"E28.MirrorCS"),sQuery(id+"F0.wireOp",EDGE,"E30.MirrorCS"),sQuery(id+"F0.wireOp",EDGE,"E32.MirrorCS"),sQuery(id+"F0.wireOp",EDGE,"E34.MirrorCS"),sQuery(id+"F0.wireOp",EDGE,"E36.MirrorCS"),sQuery(id+"F0.wireOp",EDGE,"E38.MirrorCS"),sQuery(id+"F0.wireOp",EDGE,"E40.MirrorCS"),sQuery(id+"F0.wireOp",EDGE,"E42.MirrorCS"),sQuery(id+"F0.wireOp",EDGE,"E44.MirrorCS"),sQuery(id+"F0.wireOp",EDGE,"E46.MirrorCS"),sQuery(id+"F0.wireOp",EDGE,"E48.MirrorCS"),sQuery(id+"F0.wireOp",EDGE,"E50.MirrorCS"),sQuery(id+"F0.wireOp",EDGE,"E52.MirrorCS"),sQuery(id+"F0.wireOp",EDGE,"E54.MirrorCS"),sQuery(id+"F0.wireOp",EDGE,"E56.MirrorCS"),sQuery(id+"F0.wireOp",EDGE,"E58.MirrorCS"),sQuery(id+"F0.wireOp",EDGE,"E3")])],"isStart":false});Q0=makeQuery(id+"F2.boolean.opBoolean","MERGE",FACE,{"derivedFrom":[subQ0,makeQuery(id+"F2.opPattern","COPY",FACE,{"derivedFrom":subQ0,"instanceName":"1"})]});}
            var sketch = newSketch(context, id + "F3", { "sketchPlane" : qUnion([Q0])});
            skCircle(sketch, "E114", {"center": v(0, 0) * mm, "radius": 0.64 * mm});
            skLineSegment(sketch, "E115.bottom", {"start": v(1.18, 0.25) * mm, "end": v(-1.18, 0.25) * mm});
            skLineSegment(sketch, "E115.top", {"start": v(1.18, -0.25) * mm, "end": v(-1.18, -0.25) * mm});
            skLineSegment(sketch, "E115.left", {"start": v(1.18, 0.25) * mm, "end": v(1.18, -0.25) * mm});
            skLineSegment(sketch, "E115.right", {"start": v(-1.18, 0.25) * mm, "end": v(-1.18, -0.25) * mm});
            skLineSegment(sketch, "E116.bottom", {"start": v(0.25, 1.07) * mm, "end": v(-0.25, 1.07) * mm});
            skLineSegment(sketch, "E116.top", {"start": v(0.25, -1.07) * mm, "end": v(-0.25, -1.07) * mm});
            skLineSegment(sketch, "E116.left", {"start": v(0.25, 1.07) * mm, "end": v(0.25, -1.07) * mm});
            skLineSegment(sketch, "E116.right", {"start": v(-0.25, 1.07) * mm, "end": v(-0.25, -1.07) * mm});
            skSolve(sketch);
        }
        {
            var Q0;
            {var subQ0=sQuery(id+"F3.wireOp",EDGE,"E116.left");var subQ1=sQuery(id+"F3.wireOp",EDGE,"E114");var subQ2=makeQuery(id+"F3.imprint","INTERSECT",VERTEX,{"disambiguationData":[OD(0.0)],"derivedFrom":[subQ1,subQ0]});Q0=makeQuery(id+"F3.imprint","IMPRINT",FACE,{"disambiguationData":[TD([[makeQuery(id+"F3.imprint","IMPRINT",EDGE,{"disambiguationData":[TD([[subQ2,-1.0]])],"derivedFrom":subQ1}),1.0]])]});}
            var Q1;
            {var subQ0=sQuery(id+"F3.wireOp",EDGE,"E115.bottom");var subQ1=sQuery(id+"F3.wireOp",EDGE,"E114");var subQ2=makeQuery(id+"F3.imprint","INTERSECT",VERTEX,{"disambiguationData":[OD(1.0)],"derivedFrom":[subQ1,subQ0]});Q1=makeQuery(id+"F3.imprint","IMPRINT",FACE,{"disambiguationData":[TD([[makeQuery(id+"F3.imprint","IMPRINT",EDGE,{"disambiguationData":[TD([[subQ2,-1.0]])],"derivedFrom":subQ1}),1.0]])]});}
            var Q2;
            {var subQ0=sQuery(id+"F3.wireOp",EDGE,"E116.left");var subQ1=sQuery(id+"F3.wireOp",EDGE,"E115.bottom");var subQ2=makeQuery(id+"F3.imprint","INTERSECT",VERTEX,{"derivedFrom":[subQ1,subQ0]});Q2=makeQuery(id+"F3.imprint","IMPRINT",FACE,{"disambiguationData":[TD([[makeQuery(id+"F3.imprint","IMPRINT",EDGE,{"disambiguationData":[TD([[subQ2,-1.0]])],"derivedFrom":subQ1}),1.0]])]});}
            var Q3;
            {var subQ0=sQuery(id+"F3.wireOp",EDGE,"E115.bottom");var subQ1=sQuery(id+"F3.wireOp",EDGE,"E114");var subQ2=makeQuery(id+"F3.imprint","INTERSECT",VERTEX,{"disambiguationData":[OD(0.0)],"derivedFrom":[subQ1,subQ0]});Q3=makeQuery(id+"F3.imprint","IMPRINT",FACE,{"disambiguationData":[TD([[makeQuery(id+"F3.imprint","IMPRINT",EDGE,{"disambiguationData":[TD([[subQ2,1.0]])],"derivedFrom":subQ1}),1.0]])]});}
            var Q4;
            {var subQ0=sQuery(id+"F3.wireOp",EDGE,"E116.right");var subQ1=sQuery(id+"F3.wireOp",EDGE,"E114");var subQ2=makeQuery(id+"F3.imprint","INTERSECT",VERTEX,{"disambiguationData":[OD(1.0)],"derivedFrom":[subQ1,subQ0]});Q4=makeQuery(id+"F3.imprint","IMPRINT",FACE,{"disambiguationData":[TD([[makeQuery(id+"F3.imprint","IMPRINT",EDGE,{"disambiguationData":[TD([[subQ2,-1.0]])],"derivedFrom":subQ1}),1.0]])]});}
            var Q5;
            {var subQ0=sQuery(id+"F3.wireOp",EDGE,"E116.left");var subQ1=sQuery(id+"F3.wireOp",EDGE,"E114");var subQ2=makeQuery(id+"F3.imprint","INTERSECT",VERTEX,{"disambiguationData":[OD(0.0)],"derivedFrom":[subQ1,subQ0]});Q5=makeQuery(id+"F3.imprint","IMPRINT",FACE,{"disambiguationData":[TD([[makeQuery(id+"F3.imprint","IMPRINT",EDGE,{"disambiguationData":[TD([[subQ2,1.0]])],"derivedFrom":subQ1}),1.0]])]});}
            var Q6;
            {var subQ0=sQuery(id+"F3.wireOp",EDGE,"E116.right");var subQ1=sQuery(id+"F3.wireOp",EDGE,"E114");var subQ2=makeQuery(id+"F3.imprint","INTERSECT",VERTEX,{"disambiguationData":[OD(0.0)],"derivedFrom":[subQ1,subQ0]});Q6=makeQuery(id+"F3.imprint","IMPRINT",FACE,{"disambiguationData":[TD([[makeQuery(id+"F3.imprint","IMPRINT",EDGE,{"disambiguationData":[TD([[subQ2,-1.0]])],"derivedFrom":subQ1}),1.0]])]});}
            var Q7;
            {var subQ0=sQuery(id+"F3.wireOp",EDGE,"E115.top");var subQ1=sQuery(id+"F3.wireOp",EDGE,"E114");var subQ2=makeQuery(id+"F3.imprint","INTERSECT",VERTEX,{"disambiguationData":[OD(0.0)],"derivedFrom":[subQ1,subQ0]});Q7=makeQuery(id+"F3.imprint","IMPRINT",FACE,{"disambiguationData":[TD([[makeQuery(id+"F3.imprint","IMPRINT",EDGE,{"disambiguationData":[TD([[subQ2,-1.0]])],"derivedFrom":subQ1}),1.0]])]});}
            var Q8;
            {var subQ0=sQuery(id+"F3.wireOp",EDGE,"E116.left");var subQ1=sQuery(id+"F3.wireOp",EDGE,"E114");var subQ2=makeQuery(id+"F3.imprint","INTERSECT",VERTEX,{"disambiguationData":[OD(1.0)],"derivedFrom":[subQ1,subQ0]});Q8=makeQuery(id+"F3.imprint","IMPRINT",FACE,{"disambiguationData":[TD([[makeQuery(id+"F3.imprint","IMPRINT",EDGE,{"disambiguationData":[TD([[subQ2,-1.0]])],"derivedFrom":subQ1}),1.0]])]});}
            extrude(context, id + "F4", {"entities" : qUnion([Q0, Q1, Q2, Q3, Q4, Q5, Q6, Q7, Q8]), "operationType" : NewBodyOperationType.ADD, "depth" : 19.05 * mm});
        }
        {
            var Q0;
            {var subQ0=makeQuery(id+"F1.opExtrude","CAP_FACE",FACE,{"disambiguationData":[OSD([sQuery(id+"F0.wireOp",EDGE,"E4"),sQuery(id+"F0.wireOp",EDGE,"E5"),sQuery(id+"F0.wireOp",EDGE,"E10"),sQuery(id+"F0.wireOp",EDGE,"E11"),sQuery(id+"F0.wireOp",EDGE,"E12.MirrorCS"),sQuery(id+"F0.wireOp",EDGE,"E14.MirrorCS"),sQuery(id+"F0.wireOp",EDGE,"E15.MirrorCS"),sQuery(id+"F0.wireOp",EDGE,"E18.MirrorCS"),sQuery(id+"F0.wireOp",EDGE,"E20.MirrorCS"),sQuery(id+"F0.wireOp",EDGE,"E22.MirrorCS"),sQuery(id+"F0.wireOp",EDGE,"E24.MirrorCS"),sQuery(id+"F0.wireOp",EDGE,"E26.MirrorCS"),sQuery(id+"F0.wireOp",EDGE,"E28.MirrorCS"),sQuery(id+"F0.wireOp",EDGE,"E30.MirrorCS"),sQuery(id+"F0.wireOp",EDGE,"E32.MirrorCS"),sQuery(id+"F0.wireOp",EDGE,"E34.MirrorCS"),sQuery(id+"F0.wireOp",EDGE,"E36.MirrorCS"),sQuery(id+"F0.wireOp",EDGE,"E38.MirrorCS"),sQuery(id+"F0.wireOp",EDGE,"E40.MirrorCS"),sQuery(id+"F0.wireOp",EDGE,"E42.MirrorCS"),sQuery(id+"F0.wireOp",EDGE,"E44.MirrorCS"),sQuery(id+"F0.wireOp",EDGE,"E46.MirrorCS"),sQuery(id+"F0.wireOp",EDGE,"E48.MirrorCS"),sQuery(id+"F0.wireOp",EDGE,"E50.MirrorCS"),sQuery(id+"F0.wireOp",EDGE,"E52.MirrorCS"),sQuery(id+"F0.wireOp",EDGE,"E54.MirrorCS"),sQuery(id+"F0.wireOp",EDGE,"E56.MirrorCS"),sQuery(id+"F0.wireOp",EDGE,"E58.MirrorCS"),sQuery(id+"F0.wireOp",EDGE,"E3")])],"isStart":true});Q0=makeQuery(id+"F2.boolean.opBoolean","MERGE",FACE,{"derivedFrom":[subQ0,makeQuery(id+"F2.opPattern","COPY",FACE,{"derivedFrom":subQ0,"instanceName":"1"})]});}
            var sketch = newSketch(context, id + "F5", { "sketchPlane" : qUnion([Q0])});
            skCircle(sketch, "E117", {"center": v(0, 0) * mm, "radius": 8.9 * mm});
            skLineSegment(sketch, "E118", {"start": v(0, 0) * mm, "end": v(-1.14, 10.1) * mm});
            skCircle(sketch, "E119", {"center": v(-1, 8.83) * mm, "radius": 0.64 * mm});
            skSolve(sketch);
        }
        {
            var Q0;
            {var subQ0=sQuery(id+"F5.wireOp",EDGE,"E118");var subQ1=sQuery(id+"F5.wireOp",EDGE,"E117");var subQ2=makeQuery(id+"F5.imprint","INTERSECT",VERTEX,{"derivedFrom":[subQ1,subQ0]});Q0=makeQuery(id+"F5.imprint","IMPRINT",FACE,{"disambiguationData":[TD([[makeQuery(id+"F5.imprint","IMPRINT",EDGE,{"disambiguationData":[TD([[subQ2,-1.0]])],"derivedFrom":subQ1}),-1.0]])]});}
            var Q1;
            {var subQ0=sQuery(id+"F5.wireOp",EDGE,"E119");var subQ1=sQuery(id+"F5.wireOp",EDGE,"E117");var subQ2=makeQuery(id+"F5.imprint","INTERSECT",VERTEX,{"disambiguationData":[OD(0.0)],"derivedFrom":[subQ1,subQ0]});Q1=makeQuery(id+"F5.imprint","IMPRINT",FACE,{"disambiguationData":[TD([[makeQuery(id+"F5.imprint","IMPRINT",EDGE,{"disambiguationData":[TD([[subQ2,-1.0]])],"derivedFrom":subQ1}),-1.0]])]});}
            var Q2;
            {var subQ0=sQuery(id+"F5.wireOp",EDGE,"E119");var subQ1=sQuery(id+"F5.wireOp",EDGE,"E117");var subQ2=makeQuery(id+"F5.imprint","INTERSECT",VERTEX,{"disambiguationData":[OD(0.0)],"derivedFrom":[subQ1,subQ0]});Q2=makeQuery(id+"F5.imprint","IMPRINT",FACE,{"disambiguationData":[TD([[makeQuery(id+"F5.imprint","IMPRINT",EDGE,{"disambiguationData":[TD([[subQ2,-1.0]])],"derivedFrom":subQ1}),1.0]])]});}
            var Q3;
            {var subQ0=sQuery(id+"F5.wireOp",EDGE,"E118");var subQ1=sQuery(id+"F5.wireOp",EDGE,"E117");var subQ2=makeQuery(id+"F5.imprint","INTERSECT",VERTEX,{"derivedFrom":[subQ1,subQ0]});Q3=makeQuery(id+"F5.imprint","IMPRINT",FACE,{"disambiguationData":[TD([[makeQuery(id+"F5.imprint","IMPRINT",EDGE,{"disambiguationData":[TD([[subQ2,-1.0]])],"derivedFrom":subQ1}),1.0]])]});}
            extrude(context, id + "F6", {"entities" : qUnion([Q0, Q1, Q2, Q3]), "operationType" : NewBodyOperationType.REMOVE, "oppositeDirection" : true, "depth" : 25.4 * mm});
        }
    });
